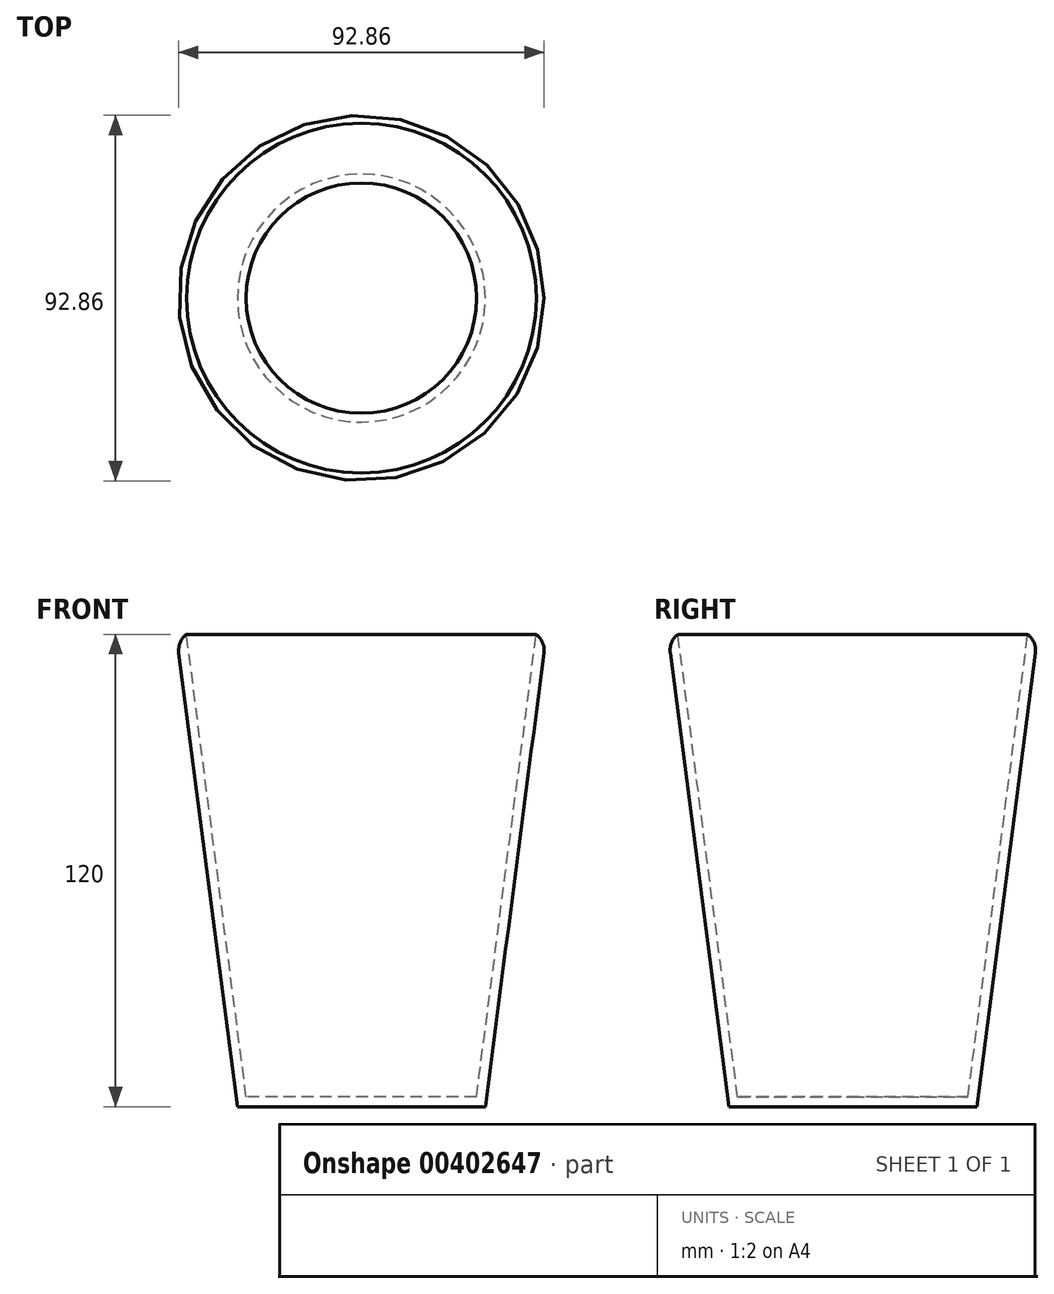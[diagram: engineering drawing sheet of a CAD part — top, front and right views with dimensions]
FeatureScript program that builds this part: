
annotation { "Feature Type Name" : "Feature", "Feature Type Description" : "" }
export const myFeature = defineFeature(function(context is Context, id is Id, definition is map)
    precondition{}
    {
        {
            var Q0;
            Q0=qCreatedBy(makeId("Top.planeOp"),FACE);
            var sketch = newSketch(context, id + "F0", { "sketchPlane" : qUnion([Q0])});
            skCircle(sketch, "E0", {"center": v(0, 0) * mm, "radius": 31.5 * mm});
            skSolve(sketch);
        }
        {
            var Q0;
            Q0=qCreatedBy(makeId("Top.planeOp"),FACE);
            cPlane(context, id + "F1", {"entities" : qUnion([Q0]), "cplaneType" : CPlaneType.OFFSET, "offset" : 120 * mm, "width" : 152.4 * mm, "height" : 152.4 * mm});
        }
        {
            var Q0;
            Q0=qCreatedBy(id+"F1.planeOp",FACE);
            var sketch = newSketch(context, id + "F2", { "sketchPlane" : qUnion([Q0])});
            skCircle(sketch, "E1", {"center": v(0, 0) * mm, "radius": 47 * mm});
            skSolve(sketch);
        }
        {
            var Q0;
            Q0=makeQuery(id+"F2.imprint","IMPRINT",FACE,{"disambiguationData":[TD([[makeQuery(id+"F2.imprint","IMPRINT",EDGE,{"derivedFrom":sQuery(id+"F2.wireOp",EDGE,"E1")}),1.0]])]});
            var Q1;
            Q1=makeQuery(id+"F0.imprint","IMPRINT",FACE,{"disambiguationData":[TD([[makeQuery(id+"F0.imprint","IMPRINT",EDGE,{"derivedFrom":sQuery(id+"F0.wireOp",EDGE,"E0")}),1.0]])]});
            loft(context, id + "F3", {"sheetProfilesArray" : [{ "sheetProfileEntities" : qUnion([Q0]) }, { "sheetProfileEntities" : qUnion([Q1]) }]});
        }
        {
            var Q0;
            Q0=makeQuery(id+"F3.opLoft","CAP_FACE",FACE,{"disambiguationData":[OSD([makeQuery(id+"F2.imprint","IMPRINT",FACE,{"disambiguationData":[TD([[makeQuery(id+"F2.imprint","IMPRINT",EDGE,{"derivedFrom":sQuery(id+"F2.wireOp",EDGE,"E1")}),1.0]])]})])],"isStart":true});
            shell(context, id + "F4", {"entities" : qUnion([Q0]), "thickness" : 2.54 * mm});
        }
        {
            var Q0;
            Q0=makeQuery(id+"F3.opLoft","MID_CAP_EDGE",EDGE,{"disambiguationData":[OSD([sQuery(id+"F2.wireOp",EDGE,"E1")])],"capPos":0.0});
            fillet(context, id + "F5", {"entities" : qUnion([Q0]), "radius" : 5.08 * mm, "tangentPropagation" : true, "allowEdgeOverflow" : false});
        }
    });
